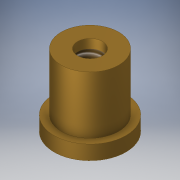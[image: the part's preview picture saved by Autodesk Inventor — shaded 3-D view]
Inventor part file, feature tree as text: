
AUTODESK INVENTOR PART (.ipt)
format: ipt  version: 2018 (Build 220112000, 112)  size: 117,248 bytes
history: native  units: in
note: dims shown in document units (in); Inventor stores cm internally (conversion verified against a paired STEP export)
features: sketch x3, extrude x2, hole x1
ambient origin geometry x8: Origin, YZ Plane, XZ Plane, XY Plane, X Axis, Y Axis, Z Axis, Center Point
bodies: Solid1 (feature_tree)
feature tree (6):
  extrude  "Extrusion1"  Depth=0.375in TaperAngle=0.0deg
  extrude  "Extrusion2"  Depth=0.3in
  hole  "Hole1"  [1 undecoded]
  sketch  "Sketch1"  dims[d0=0.375in d1=0.375in d2=0.0in]
  sketch  "Sketch2"  dims[d3=0.5in d4=0.3in]
  sketch  "Sketch3"  dims[d5=0.3in d6=0.0in d7=0.13in d8=0.328in d9=0.375in d10=0.25in d11=0.5635in d12=0.484in d13=0.8108in]
note: 1 required parameter value undecoded (feature->parameter linkage not recoverable at this tier; creation-order binding heuristic only, values carry confidence <= 0.55)
